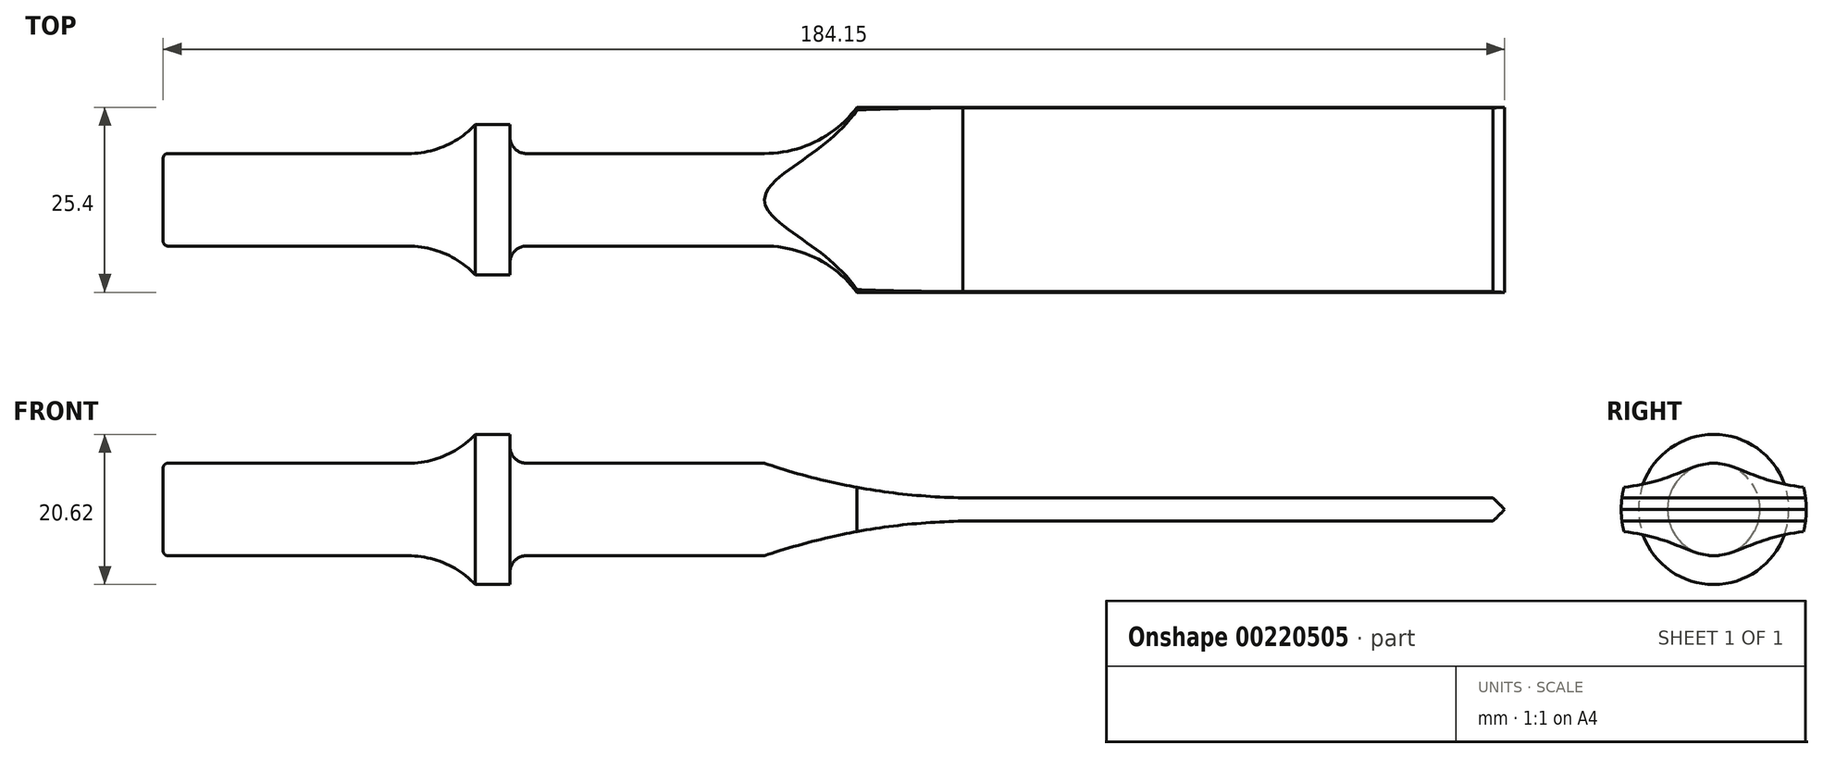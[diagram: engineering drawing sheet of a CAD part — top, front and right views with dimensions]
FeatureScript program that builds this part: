
annotation { "Feature Type Name" : "Feature", "Feature Type Description" : "" }
export const myFeature = defineFeature(function(context is Context, id is Id, definition is map)
    precondition{}
    {
        {
            var Q0;
            Q0=qCreatedBy(makeId("Front.planeOp"),FACE);
            var sketch = newSketch(context, id + "F0", { "sketchPlane" : qUnion([Q0])});
            skLineSegment(sketch, "E0", {"start": v(0, 0) * mm, "end": v(184.15, 0) * mm});
            skLineSegment(sketch, "E1", {"start": v(0, 0) * mm, "end": v(0, 5.69) * mm});
            skLineSegment(sketch, "E2", {"start": v(0.66, 6.35) * mm, "end": v(33.63, 6.35) * mm});
            skLineSegment(sketch, "E3", {"start": v(42.85, 10.31) * mm, "end": v(47.6, 10.31) * mm});
            skLineSegment(sketch, "E4", {"start": v(47.6, 10.31) * mm, "end": v(47.6, 8.64) * mm});
            skLineSegment(sketch, "E5", {"start": v(184.15, 0) * mm, "end": v(184.15, 12.7) * mm});
            skLineSegment(sketch, "E6.0", {"start": v(82.55, 0) * mm, "end": v(82.55, 12.7) * mm, "construction": true});
            skLineSegment(sketch, "E7.0", {"start": v(95.25, 0) * mm, "end": v(95.25, 12.7) * mm, "construction": true});
            skLineSegment(sketch, "E8", {"start": v(184.15, 12.7) * mm, "end": v(82.55, 12.7) * mm});
            skLineSegment(sketch, "E9.trimOffspring", {"start": v(49.89, 6.35) * mm, "end": v(82.55, 6.35) * mm});
            skArc(sketch, "E10", {"start": v(82.55, 6.35) * mm, "mid": v(89.65, 8.03) * mm, "end": v(95.25, 12.7) * mm});
            skPoint(sketch, "E11.orphan", {"position": v(47.6, 0) * mm});
            skArc(sketch, "E12", {"start": v(33.63, 6.35) * mm, "mid": v(38.65, 7.38) * mm, "end": v(42.85, 10.31) * mm});
            skPoint(sketch, "E13.visualSharp", {"position": v(0, 6.35) * mm});
            skArc(sketch, "E13.filletArc", {"start": v(0.66, 6.35) * mm, "mid": v(0.2, 6.16) * mm, "end": v(0, 5.69) * mm});
            skPoint(sketch, "E14.visualSharp", {"position": v(47.6, 6.35) * mm});
            skArc(sketch, "E14.filletArc", {"start": v(47.6, 8.64) * mm, "mid": v(48.27, 7.02) * mm, "end": v(49.89, 6.35) * mm});
            skPoint(sketch, "E15.start.orphan", {"position": v(42.85, 6.35) * mm});
            skSolve(sketch);
        }
        {
            var Q0;
            Q0=makeQuery(id+"F0.imprint","IMPRINT",FACE,{"disambiguationData":[TD([[makeQuery(id+"F0.imprint","IMPRINT",EDGE,{"derivedFrom":sQuery(id+"F0.wireOp",EDGE,"E0")}),1.0]])]});
            var Q1;
            Q1=sQuery(id+"F0.wireOp",EDGE,"E0");
            revolve(context, id + "F1", {"entities" : qUnion([Q0]), "axis" : qUnion([Q1]), "revolveType" : RevolveType.FULL});
        }
        {
            var Q0;
            Q0=qCreatedBy(makeId("Front.planeOp"),FACE);
            var sketch = newSketch(context, id + "F2", { "sketchPlane" : qUnion([Q0])});
            skLineSegment(sketch, "E16", {"start": v(0, 0) * mm, "end": v(184.15, 0) * mm, "construction": true});
            skLineSegment(sketch, "E17", {"start": v(184.15, 0) * mm, "end": v(184.15, 29.08) * mm, "construction": true});
            skLineSegment(sketch, "E18.0", {"start": v(82.55, 0) * mm, "end": v(82.55, 29.08) * mm, "construction": true});
            skLineSegment(sketch, "E19.0", {"start": v(0, 6.35) * mm, "end": v(184.15, 6.35) * mm, "construction": true});
            skPoint(sketch, "E20", {"position": v(82.55, 6.35) * mm});
            skLineSegment(sketch, "E21.0", {"start": v(109.75, 1.6) * mm, "end": v(182.55, 1.6) * mm});
            skArc(sketch, "E22", {"start": v(82.55, 6.35) * mm, "mid": v(96.7, 2.79) * mm, "end": v(111.26, 1.59) * mm});
            skLineSegment(sketch, "E23", {"start": v(184.15, 0) * mm, "end": v(182.55, 1.6) * mm});
            skLineSegment(sketch, "E24", {"start": v(82.55, 6.35) * mm, "end": v(82.55, 38.47) * mm});
            skLineSegment(sketch, "E25", {"start": v(82.55, 38.47) * mm, "end": v(196.87, 38.47) * mm});
            skLineSegment(sketch, "E26", {"start": v(196.87, 38.47) * mm, "end": v(184.15, 0) * mm});
            skLineSegment(sketch, "E27.MirrorCS", {"start": v(165.1, 0) * mm, "end": v(-19.05, 0) * mm, "construction": true});
            skLineSegment(sketch, "E28.MirrorCS", {"start": v(82.55, -6.35) * mm, "end": v(82.55, -38.47) * mm});
            skArc(sketch, "E29.MirrorCS", {"start": v(82.55, -6.35) * mm, "mid": v(96.7, -2.79) * mm, "end": v(111.26, -1.59) * mm});
            skLineSegment(sketch, "E30.MirrorCS", {"start": v(82.55, -38.47) * mm, "end": v(196.87, -38.47) * mm});
            skLineSegment(sketch, "E31.MirrorCS", {"start": v(109.75, -1.6) * mm, "end": v(182.55, -1.6) * mm});
            skLineSegment(sketch, "E32.MirrorCS", {"start": v(196.87, -38.47) * mm, "end": v(184.15, 0) * mm});
            skLineSegment(sketch, "E33.MirrorCS", {"start": v(184.15, 0) * mm, "end": v(182.55, -1.6) * mm});
            skSolve(sketch);
        }
        {
            var Q0;
            Q0 = qSketchRegion(id + "F2", true);
            extrude(context, id + "F3", {"entities" : qUnion([Q0]), "operationType" : NewBodyOperationType.REMOVE, "oppositeDirection" : true, "depth" : 32 * mm, "hasSecondDirection" : true, "secondDirectionOppositeDirection" : false, "secondDirectionDepth" : 27.94 * mm});
        }
    });
